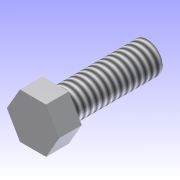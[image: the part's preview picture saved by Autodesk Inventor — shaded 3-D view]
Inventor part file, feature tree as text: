
AUTODESK INVENTOR PART (.ipt)
format: ipt  version: 2012 (Build 160160000, 160)  size: 83,456 bytes
history: native  units: in
note: dims shown in document units (in); Inventor stores cm internally (conversion verified against a paired STEP export)
features: extrude x2, sketch x1, thread x1
ambient origin geometry x8: Origin, YZ Plane, XZ Plane, XY Plane, X Axis, Y Axis, Z Axis, Center Point
bodies: Solid1 (feature_tree)
feature tree (4):
  sketch  "Sketch1"  dims[d10=0.37in d11=0.75in d12=0.0in d13=0.185in d14=0.0in d15=1.0in d16=0.0in]
  extrude  "Extrusion1"  Depth=0.75in TaperAngle=0.0deg
  extrude  "Extrusion2"  Depth=0.185in TaperAngle=0.0deg
  thread  "Thread1"  [1 undecoded]
note: 1 required parameter value undecoded (feature->parameter linkage not recoverable at this tier; creation-order binding heuristic only, values carry confidence <= 0.55)
